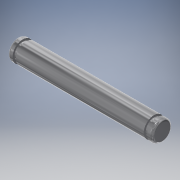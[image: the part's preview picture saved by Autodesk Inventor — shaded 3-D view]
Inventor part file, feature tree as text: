
AUTODESK INVENTOR PART (.ipt)
format: ipt  version: 2018 (Build 220112000, 112)  size: 131,072 bytes
history: native  units: mm
features: revolve x1, sketch x1
ambient origin geometry x8: Origin, YZ Plane, XZ Plane, XY Plane, X Axis, Y Axis, Z Axis, Center Point
bodies: Solid1 (feature_tree)
feature tree (2):
  revolve  "Revolution1"  [1 undecoded]
  sketch  "Sketch1"  dims[d0=25.0mm d1=0.65mm d2=1.0mm d3=2.0mm d4=1.6mm d5=1.6mm d6=0.5mm d7=1.0mm d8=0.5mm d9=90.0deg]
note: 1 required parameter value undecoded (feature->parameter linkage not recoverable at this tier; creation-order binding heuristic only, values carry confidence <= 0.55)
